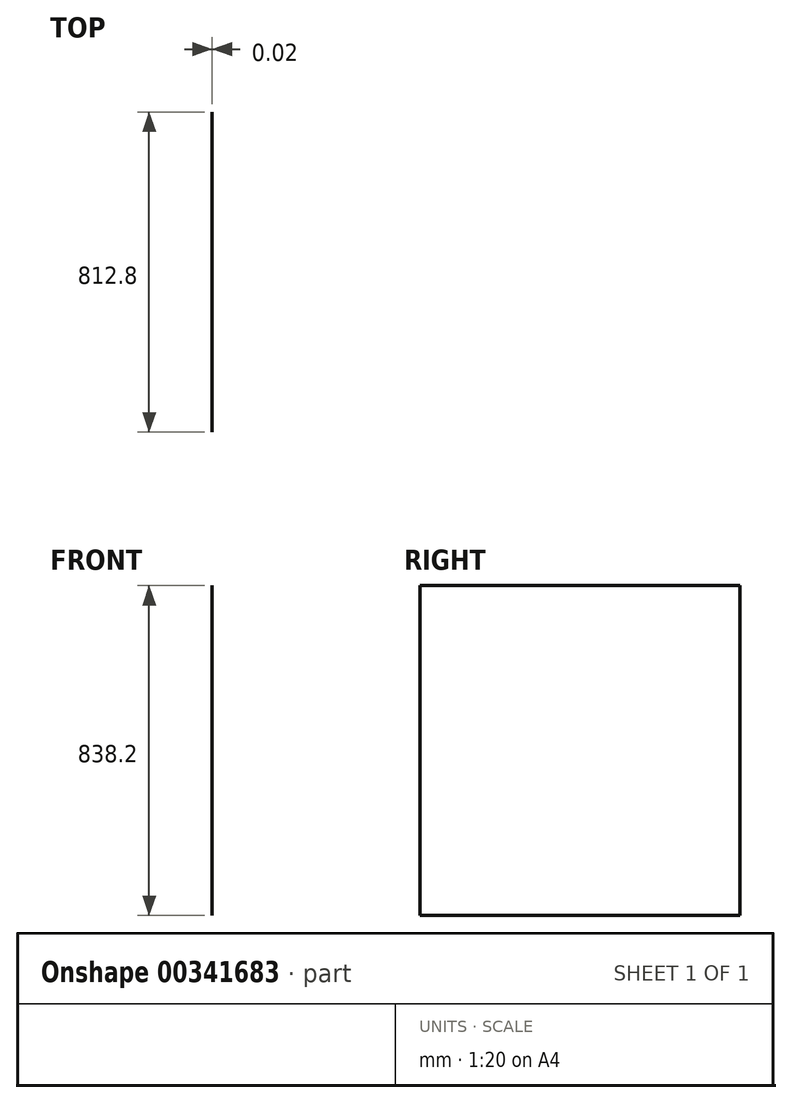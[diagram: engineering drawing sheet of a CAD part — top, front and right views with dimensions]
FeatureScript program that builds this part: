
annotation { "Feature Type Name" : "Feature", "Feature Type Description" : "" }
export const myFeature = defineFeature(function(context is Context, id is Id, definition is map)
    precondition{}
    {
        {
            var Q0;
            Q0=qCreatedBy(makeId("Right.planeOp"),FACE);
            var sketch = newSketch(context, id + "F0", { "sketchPlane" : qUnion([Q0])});
            skLineSegment(sketch, "E0.bottom", {"start": v(413.3, 460.2) * mm, "end": v(-399.5, 460.2) * mm});
            skLineSegment(sketch, "E0.top", {"start": v(413.3, -378) * mm, "end": v(-399.5, -378) * mm});
            skLineSegment(sketch, "E0.left", {"start": v(413.3, 460.2) * mm, "end": v(413.3, -378) * mm});
            skLineSegment(sketch, "E0.right", {"start": v(-399.5, 460.2) * mm, "end": v(-399.5, -378) * mm});
            skSolve(sketch);
        }
        {
            var Q0;
            Q0=makeQuery(id+"F0.imprint","IMPRINT",FACE,{"disambiguationData":[TD([[makeQuery(id+"F0.imprint","IMPRINT",EDGE,{"derivedFrom":sQuery(id+"F0.wireOp",EDGE,"E0.bottom")}),1.0]])]});
            extrude(context, id + "F1", {"entities" : qUnion([Q0]), "depth" : 1 / 50.8 * mm});
        }
    });
